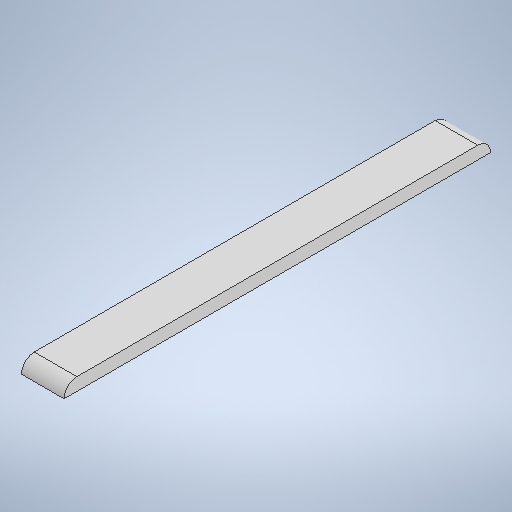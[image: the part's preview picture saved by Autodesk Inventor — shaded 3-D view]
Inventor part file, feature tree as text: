
AUTODESK INVENTOR PART (.ipt)
format: ipt  version: 2025.2 (Build 292293000, 293)  size: 230,912 bytes
history: native  units: mm
features: extrude x1, fillet x1, sketch x1
ambient origin geometry x8: Origin, YZ Plane, XZ Plane, XY Plane, X Axis, Y Axis, Z Axis, Center Point
bodies: Solid1 (feature_tree)
feature tree (3):
  extrude  "Extrusion1"  Depth=100.0mm
  fillet  "Fillet1"  Radius=3.0mm
  sketch  "Sketch1"  dims[d0=10.0mm d1=100.0mm d2=3.0mm d3=0.0mm d4=3.0mm]
